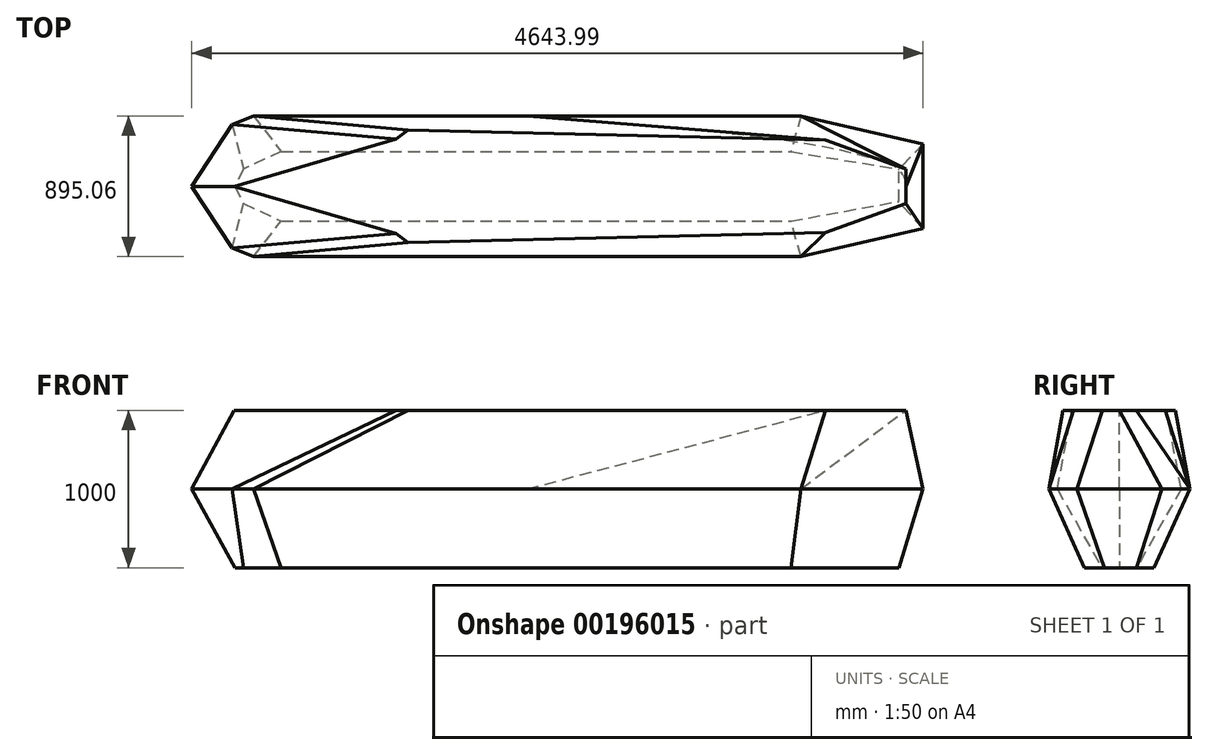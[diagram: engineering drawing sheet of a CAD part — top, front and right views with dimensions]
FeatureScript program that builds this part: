
annotation { "Feature Type Name" : "Feature", "Feature Type Description" : "" }
export const myFeature = defineFeature(function(context is Context, id is Id, definition is map)
    precondition{}
    {
        {
            var Q0;
            Q0=qCreatedBy(makeId("Top.planeOp"),FACE);
            var sketch = newSketch(context, id + "F0", { "sketchPlane" : qUnion([Q0])});
            skLineSegment(sketch, "E0", {"start": v(-849.8, 0) * mm, "end": v(-591.7, -393.6) * mm});
            skLineSegment(sketch, "E1", {"start": v(-591.7, -393.6) * mm, "end": v(-456.87, -447.53) * mm});
            skLineSegment(sketch, "E2", {"start": v(-456.87, -447.53) * mm, "end": v(3020.9, -447.53) * mm});
            skLineSegment(sketch, "E3", {"start": v(3020.9, -447.53) * mm, "end": v(3794.2, -269.5) * mm});
            skLineSegment(sketch, "E4.MirrorCS", {"start": v(-849.8, 0) * mm, "end": v(-591.7, 393.6) * mm});
            skLineSegment(sketch, "E5.MirrorCS", {"start": v(-456.87, 447.53) * mm, "end": v(3020.9, 447.53) * mm});
            skLineSegment(sketch, "E6.MirrorCS", {"start": v(3020.9, 447.53) * mm, "end": v(3794.2, 269.5) * mm});
            skLineSegment(sketch, "E7.MirrorCS", {"start": v(-591.7, 393.6) * mm, "end": v(-456.87, 447.53) * mm});
            skLineSegment(sketch, "E8", {"start": v(3794.2, -269.5) * mm, "end": v(3794.2, 269.5) * mm});
            skSolve(sketch);
        }
        {
            var Q0;
            Q0=makeQuery(id+"F0.imprint","IMPRINT",FACE,{"disambiguationData":[TD([[makeQuery(id+"F0.imprint","IMPRINT",EDGE,{"derivedFrom":sQuery(id+"F0.wireOp",EDGE,"E0")}),1.0]])]});
            cPlane(context, id + "F1", {"entities" : qUnion([Q0]), "cplaneType" : CPlaneType.OFFSET, "offset" : 500 * mm, "oppositeDirection" : true, "width" : 150 * mm, "height" : 150 * mm});
        }
        {
            var Q0;
            Q0=qCreatedBy(id+"F1.planeOp",FACE);
            var sketch = newSketch(context, id + "F2", { "sketchPlane" : qUnion([Q0])});
            skLineSegment(sketch, "E9.bottom", {"start": v(-280.9, -221.1) * mm, "end": v(2955, -221.1) * mm});
            skLineSegment(sketch, "E9.top", {"start": v(-280.9, 221.1) * mm, "end": v(2955, 221.1) * mm});
            skLineSegment(sketch, "E9.right", {"start": v(3640.74, -95.8) * mm, "end": v(3642.8, 107.6) * mm});
            skLineSegment(sketch, "E10", {"start": v(-575.2, 0) * mm, "end": v(-520.64, -110.55) * mm});
            skLineSegment(sketch, "E11", {"start": v(-520.64, 110.55) * mm, "end": v(-575.2, 0) * mm});
            skLineSegment(sketch, "E12", {"start": v(-520.64, -110.55) * mm, "end": v(-280.9, -221.1) * mm});
            skLineSegment(sketch, "E13", {"start": v(-280.9, 221.1) * mm, "end": v(-520.64, 110.55) * mm});
            skLineSegment(sketch, "E14", {"start": v(2955, -221.1) * mm, "end": v(3640.74, -95.8) * mm});
            skLineSegment(sketch, "E15", {"start": v(2955, 221.1) * mm, "end": v(3642.8, 107.6) * mm});
            skSolve(sketch);
        }
        {
            var Q0;
            Q0=makeQuery(id+"F0.imprint","IMPRINT",FACE,{"disambiguationData":[TD([[makeQuery(id+"F0.imprint","IMPRINT",EDGE,{"derivedFrom":sQuery(id+"F0.wireOp",EDGE,"E0")}),1.0]])]});
            var Q1;
            Q1=makeQuery(id+"F2.imprint","IMPRINT",FACE,{"disambiguationData":[TD([[makeQuery(id+"F2.imprint","IMPRINT",EDGE,{"derivedFrom":sQuery(id+"F2.wireOp",EDGE,"E9.bottom")}),1.0]])]});
            loft(context, id + "F3", {"sheetProfilesArray" : [{ "sheetProfileEntities" : qUnion([Q0]) }, { "sheetProfileEntities" : qUnion([Q1]) }]});
        }
        {
            var Q0;
            Q0=makeQuery(id+"F3.opLoft","CAP_FACE",FACE,{"disambiguationData":[OSD([makeQuery(id+"F0.imprint","IMPRINT",FACE,{"disambiguationData":[TD([[makeQuery(id+"F0.imprint","IMPRINT",EDGE,{"derivedFrom":sQuery(id+"F0.wireOp",EDGE,"E0")}),1.0]])]})])],"isStart":true});
            cPlane(context, id + "F4", {"entities" : qUnion([Q0]), "cplaneType" : CPlaneType.OFFSET, "offset" : 500 * mm, "width" : 150 * mm, "height" : 150 * mm});
        }
        {
            var Q0;
            Q0=qCreatedBy(id+"F4.planeOp",FACE);
            var sketch = newSketch(context, id + "F5", { "sketchPlane" : qUnion([Q0])});
            skLineSegment(sketch, "E16", {"start": v(-581.25, 0) * mm, "end": v(448.5, 299.84) * mm});
            skLineSegment(sketch, "E17", {"start": v(448.5, 299.84) * mm, "end": v(524.45, 357.77) * mm});
            skLineSegment(sketch, "E18", {"start": v(524.45, 357.77) * mm, "end": v(3176.2, 292.4) * mm});
            skLineSegment(sketch, "E19", {"start": v(3176.2, 292.4) * mm, "end": v(3686.44, 108.7) * mm});
            skLineSegment(sketch, "E20", {"start": v(3686.44, 108.7) * mm, "end": v(3686.44, 0) * mm});
            skLineSegment(sketch, "E21.MirrorCS", {"start": v(-581.25, 0) * mm, "end": v(448.5, -299.84) * mm});
            skLineSegment(sketch, "E22.MirrorCS", {"start": v(448.5, -299.84) * mm, "end": v(524.45, -357.77) * mm});
            skLineSegment(sketch, "E23.MirrorCS", {"start": v(524.45, -357.77) * mm, "end": v(3176.2, -292.4) * mm});
            skLineSegment(sketch, "E24.MirrorCS", {"start": v(3176.2, -292.4) * mm, "end": v(3686.44, -108.7) * mm});
            skLineSegment(sketch, "E25.MirrorCS", {"start": v(3686.44, -108.7) * mm, "end": v(3686.44, 0) * mm});
            skSolve(sketch);
        }
        {
            var Q1;
            Q1=makeQuery(id+"F3.opLoft","CAP_FACE",FACE,{"disambiguationData":[OSD([makeQuery(id+"F0.imprint","IMPRINT",FACE,{"disambiguationData":[TD([[makeQuery(id+"F0.imprint","IMPRINT",EDGE,{"derivedFrom":sQuery(id+"F0.wireOp",EDGE,"E0")}),1.0]])]})])],"isStart":true});
            var Q2;
            Q2=makeQuery(id+"F5.imprint","IMPRINT",FACE,{"disambiguationData":[TD([[makeQuery(id+"F5.imprint","IMPRINT",EDGE,{"derivedFrom":sQuery(id+"F5.wireOp",EDGE,"E16")}),-1.0]])]});
            loft(context, id + "F6", {"operationType" : NewBodyOperationType.ADD, "sheetProfilesArray" : [{ "sheetProfileEntities" : qUnion([Q1]) }, { "sheetProfileEntities" : qUnion([Q2]) }]});
        }
    });
